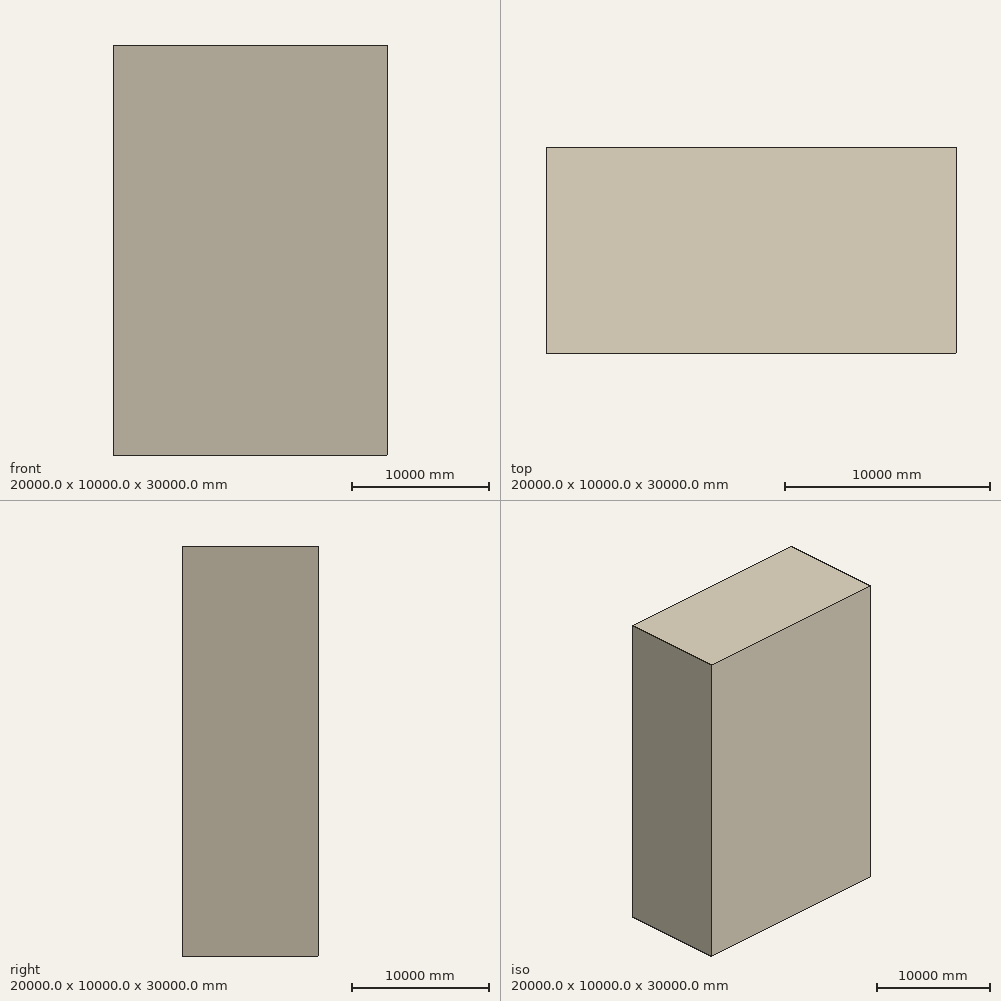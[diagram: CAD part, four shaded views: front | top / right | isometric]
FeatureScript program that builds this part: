
annotation { "Feature Type Name" : "Feature", "Feature Type Description" : "" }
export const myFeature = defineFeature(function(context is Context, id is Id, definition is map)
    precondition{}
    {
        {
            var Q0;
            Q0=qCreatedBy(makeId("Front.planeOp"),FACE);
            var sketch = newSketch(context, id + "F0", { "sketchPlane" : qUnion([Q0])});
            skLineSegment(sketch, "E0.bottom", {"start": v(0, 0) * mm, "end": v(20000, 0) * mm});
            skLineSegment(sketch, "E0.top", {"start": v(0, 30000) * mm, "end": v(20000, 30000) * mm});
            skLineSegment(sketch, "E0.left", {"start": v(0, 0) * mm, "end": v(0, 30000) * mm});
            skLineSegment(sketch, "E0.right", {"start": v(20000, 0) * mm, "end": v(20000, 30000) * mm});
            skSolve(sketch);
        }
        {
            var Q0;
            Q0=makeQuery(id+"F0.imprint","IMPRINT",FACE,{"disambiguationData":[TD([[makeQuery(id+"F0.imprint","IMPRINT",EDGE,{"derivedFrom":sQuery(id+"F0.wireOp",EDGE,"E0.bottom")}),1.0]])]});
            extrude(context, id + "F1", {"entities" : qUnion([Q0]), "oppositeDirection" : true, "depth" : 10000 * mm});
        }
    });
